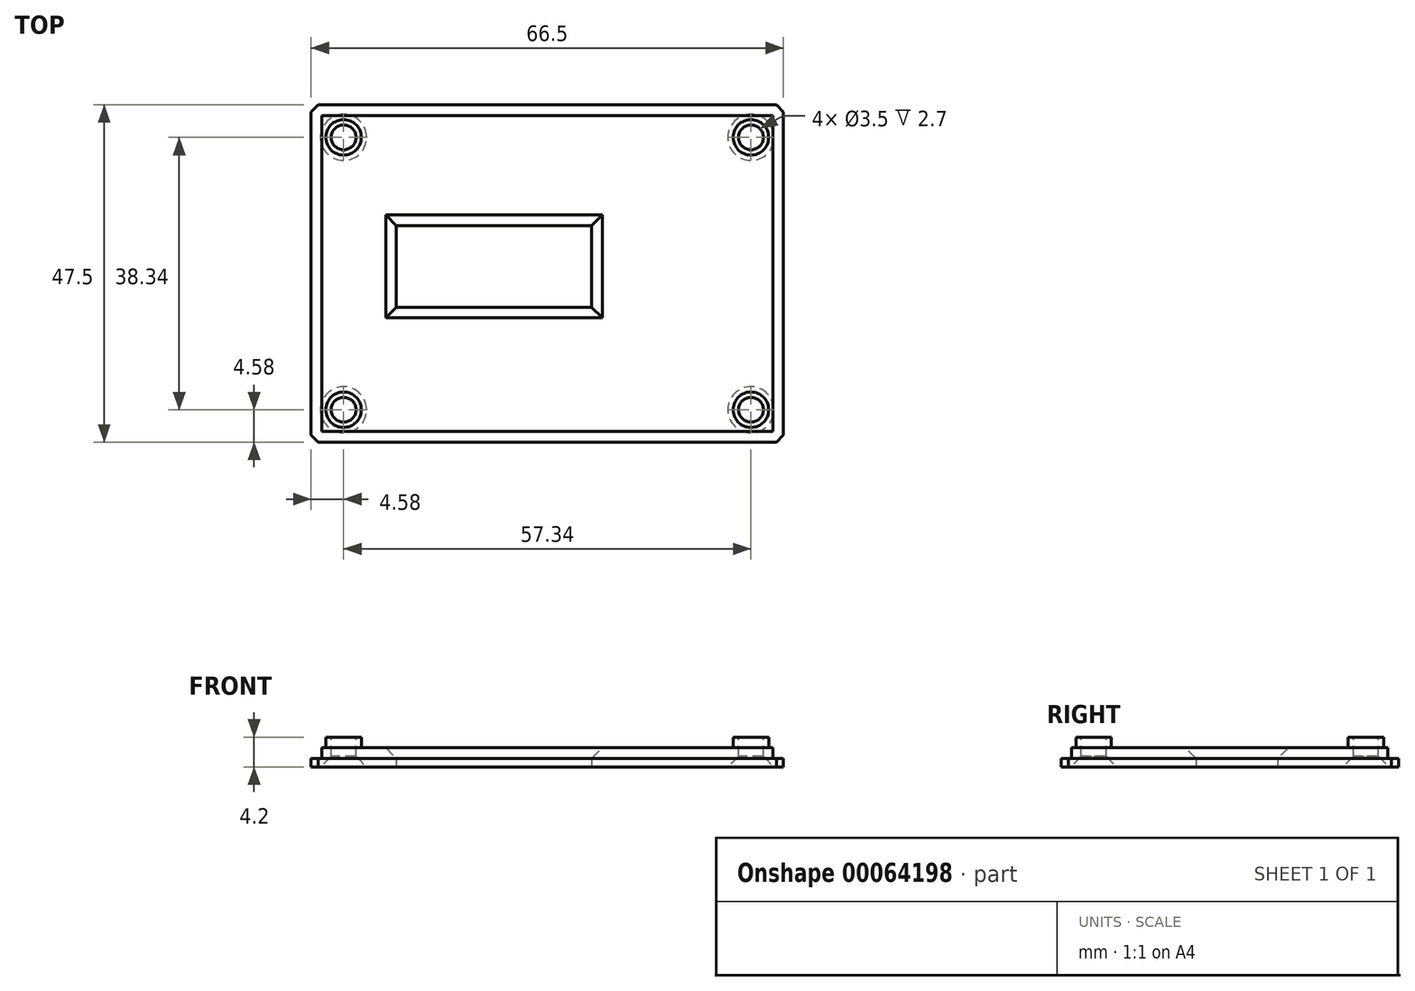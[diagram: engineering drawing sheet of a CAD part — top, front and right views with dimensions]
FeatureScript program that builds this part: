
annotation { "Feature Type Name" : "Feature", "Feature Type Description" : "" }
export const myFeature = defineFeature(function(context is Context, id is Id, definition is map)
    precondition{}
    {
        {
            var Q0;
            Q0=qCreatedBy(makeId("Top.planeOp"),FACE);
            var sketch = newSketch(context, id + "F0", { "sketchPlane" : qUnion([Q0])});
            skLineSegment(sketch, "E0.rect.bottom", {"start": v(33.25, 23.75) * mm, "end": v(-33.25, 23.75) * mm});
            skLineSegment(sketch, "E0.rect.top", {"start": v(33.25, -23.75) * mm, "end": v(-33.25, -23.75) * mm});
            skLineSegment(sketch, "E0.rect.left", {"start": v(33.25, 23.75) * mm, "end": v(33.25, -23.75) * mm});
            skLineSegment(sketch, "E0.rect.right", {"start": v(-33.25, 23.75) * mm, "end": v(-33.25, -23.75) * mm});
            skPoint(sketch, "E0.rect.middle", {"position": v(0, 0) * mm});
            skSolve(sketch);
        }
        {
            var Q0;
            Q0=qSketchRegion(id+"F0",true);
            extrude(context, id + "F1", {"entities" : qUnion([Q0]), "depth" : 1.2 * mm});
        }
        {
            var Q0;
            Q0=makeQuery(id+"F1.opExtrude","CAP_FACE",FACE,{"disambiguationData":[OSD([sQuery(id+"F0.wireOp",EDGE,"E0.rect.bottom"),sQuery(id+"F0.wireOp",EDGE,"E0.rect.top"),sQuery(id+"F0.wireOp",EDGE,"E0.rect.left"),sQuery(id+"F0.wireOp",EDGE,"E0.rect.right")])],"isStart":false});
            var sketch = newSketch(context, id + "F2", { "sketchPlane" : qUnion([Q0])});
            skLineSegment(sketch, "E1.bottom", {"start": v(-31.75, 22.25) * mm, "end": v(31.75, 22.25) * mm});
            skLineSegment(sketch, "E1.top", {"start": v(-31.75, -22.25) * mm, "end": v(31.75, -22.25) * mm});
            skLineSegment(sketch, "E1.left", {"start": v(-31.75, 22.25) * mm, "end": v(-31.75, -22.25) * mm});
            skLineSegment(sketch, "E1.right", {"start": v(31.75, 22.25) * mm, "end": v(31.75, -22.25) * mm});
            skSolve(sketch);
        }
        {
            var Q0;
            Q0=qSketchRegion(id+"F2",true);
            extrude(context, id + "F3", {"entities" : qUnion([Q0]), "operationType" : NewBodyOperationType.ADD, "depth" : 1.5 * mm});
        }
        {
            var Q0;
            Q0=makeQuery(id+"F3.opExtrude","CAP_FACE",FACE,{"disambiguationData":[OSD([sQuery(id+"F2.wireOp",EDGE,"E1.bottom"),sQuery(id+"F2.wireOp",EDGE,"E1.top"),sQuery(id+"F2.wireOp",EDGE,"E1.left"),sQuery(id+"F2.wireOp",EDGE,"E1.right")])],"isStart":false});
            var sketch = newSketch(context, id + "F4", { "sketchPlane" : qUnion([Q0])});
            skCircle(sketch, "E2", {"center": v(-28.67, -19.17) * mm, "radius": 2.5 * mm});
            skCircle(sketch, "E3.0.MirrorC", {"center": v(28.67, -19.17) * mm, "radius": 2.5 * mm});
            skCircle(sketch, "E4.0.MirrorC", {"center": v(-28.67, 19.17) * mm, "radius": 2.5 * mm});
            skCircle(sketch, "E5.0.MirrorC", {"center": v(28.67, 19.17) * mm, "radius": 2.5 * mm});
            skSolve(sketch);
        }
        {
            var Q0;
            Q0=qSketchRegion(id+"F4",true);
            extrude(context, id + "F5", {"entities" : qUnion([Q0]), "operationType" : NewBodyOperationType.ADD, "depth" : 1.5 * mm});
        }
        {
            var Q0;
            Q0=makeQuery(id+"F5.opExtrude","CAP_FACE",FACE,{"disambiguationData":[OSD([sQuery(id+"F4.wireOp",EDGE,"E2")])],"isStart":false});
            var sketch = newSketch(context, id + "F6", { "sketchPlane" : qUnion([Q0])});
            skCircle(sketch, "E6", {"center": v(-28.67, -19.17) * mm, "radius": 1.75 * mm});
            skCircle(sketch, "E7.0.MirrorC", {"center": v(28.67, -19.17) * mm, "radius": 1.75 * mm});
            skCircle(sketch, "E8.0.MirrorC", {"center": v(-28.67, 19.17) * mm, "radius": 1.75 * mm});
            skCircle(sketch, "E9.0.MirrorC", {"center": v(28.67, 19.17) * mm, "radius": 1.75 * mm});
            skSolve(sketch);
        }
        {
            var Q0;
            Q0=qSketchRegion(id+"F6",true);
            extrude(context, id + "F7", {"entities" : qUnion([Q0]), "operationType" : NewBodyOperationType.REMOVE, "endBound" : BoundingType.THROUGH_ALL, "oppositeDirection" : true, "depth" : 25 * mm});
        }
        {
            var Q0;
            Q0=makeQuery(id+"F1.opExtrude","CAP_FACE",FACE,{"disambiguationData":[OSD([sQuery(id+"F0.wireOp",EDGE,"E0.rect.bottom"),sQuery(id+"F0.wireOp",EDGE,"E0.rect.top"),sQuery(id+"F0.wireOp",EDGE,"E0.rect.left"),sQuery(id+"F0.wireOp",EDGE,"E0.rect.right")])],"isStart":true});
            var sketch = newSketch(context, id + "F8", { "sketchPlane" : qUnion([Q0])});
            skLineSegment(sketch, "E10.bottom", {"start": v(-21.25, 4.75) * mm, "end": v(6.25, 4.75) * mm});
            skLineSegment(sketch, "E10.top", {"start": v(-21.25, -6.75) * mm, "end": v(6.25, -6.75) * mm});
            skLineSegment(sketch, "E10.left", {"start": v(-21.25, 4.75) * mm, "end": v(-21.25, -6.75) * mm});
            skLineSegment(sketch, "E10.right", {"start": v(6.25, 4.75) * mm, "end": v(6.25, -6.75) * mm});
            skSolve(sketch);
        }
        {
            var Q0;
            Q0=qSketchRegion(id+"F8",true);
            extrude(context, id + "F9", {"entities" : qUnion([Q0]), "operationType" : NewBodyOperationType.REMOVE, "endBound" : BoundingType.THROUGH_ALL, "oppositeDirection" : true, "depth" : 25 * mm});
        }
        {
            var Q0;
            Q0=makeQuery(id+"F7.boolean.opBoolean","INTERSECT",EDGE,{"derivedFrom":[makeQuery(id+"F1.opExtrude","CAP_FACE",FACE,{"disambiguationData":[OSD([sQuery(id+"F0.wireOp",EDGE,"E0.rect.bottom"),sQuery(id+"F0.wireOp",EDGE,"E0.rect.top"),sQuery(id+"F0.wireOp",EDGE,"E0.rect.left"),sQuery(id+"F0.wireOp",EDGE,"E0.rect.right")])],"isStart":true}),makeQuery(id+"F7.opExtrude","SWEPT_FACE",FACE,{"disambiguationData":[OSD([sQuery(id+"F6.wireOp",EDGE,"E6")])]})]});
            var Q1;
            Q1=makeQuery(id+"F7.boolean.opBoolean","INTERSECT",EDGE,{"derivedFrom":[makeQuery(id+"F1.opExtrude","CAP_FACE",FACE,{"disambiguationData":[OSD([sQuery(id+"F0.wireOp",EDGE,"E0.rect.bottom"),sQuery(id+"F0.wireOp",EDGE,"E0.rect.top"),sQuery(id+"F0.wireOp",EDGE,"E0.rect.left"),sQuery(id+"F0.wireOp",EDGE,"E0.rect.right")])],"isStart":true}),makeQuery(id+"F7.opExtrude","SWEPT_FACE",FACE,{"disambiguationData":[OSD([sQuery(id+"F6.wireOp",EDGE,"E7.0.MirrorC")])]})]});
            var Q2;
            Q2=makeQuery(id+"F7.boolean.opBoolean","INTERSECT",EDGE,{"derivedFrom":[makeQuery(id+"F1.opExtrude","CAP_FACE",FACE,{"disambiguationData":[OSD([sQuery(id+"F0.wireOp",EDGE,"E0.rect.bottom"),sQuery(id+"F0.wireOp",EDGE,"E0.rect.top"),sQuery(id+"F0.wireOp",EDGE,"E0.rect.left"),sQuery(id+"F0.wireOp",EDGE,"E0.rect.right")])],"isStart":true}),makeQuery(id+"F7.opExtrude","SWEPT_FACE",FACE,{"disambiguationData":[OSD([sQuery(id+"F6.wireOp",EDGE,"E9.0.MirrorC")])]})]});
            var Q3;
            Q3=makeQuery(id+"F7.boolean.opBoolean","INTERSECT",EDGE,{"derivedFrom":[makeQuery(id+"F1.opExtrude","CAP_FACE",FACE,{"disambiguationData":[OSD([sQuery(id+"F0.wireOp",EDGE,"E0.rect.bottom"),sQuery(id+"F0.wireOp",EDGE,"E0.rect.top"),sQuery(id+"F0.wireOp",EDGE,"E0.rect.left"),sQuery(id+"F0.wireOp",EDGE,"E0.rect.right")])],"isStart":true}),makeQuery(id+"F7.opExtrude","SWEPT_FACE",FACE,{"disambiguationData":[OSD([sQuery(id+"F6.wireOp",EDGE,"E8.0.MirrorC")])]})]});
            chamfer(context, id + "F10", {"entities" : qUnion([Q0, Q1, Q2, Q3]), "width" : 1.5 * mm, "tangentPropagation" : true});
        }
        {
            var Q0;
            Q0=makeQuery(id+"F1.opExtrude","SWEPT_EDGE",EDGE,{"disambiguationData":[OSD([sQuery(id+"F0.wireOp",EDGE,"E0.rect.top"),sQuery(id+"F0.wireOp",EDGE,"E0.rect.right")])]});
            var Q1;
            Q1=makeQuery(id+"F1.opExtrude","SWEPT_EDGE",EDGE,{"disambiguationData":[OSD([sQuery(id+"F0.wireOp",EDGE,"E0.rect.bottom"),sQuery(id+"F0.wireOp",EDGE,"E0.rect.right")])]});
            var Q2;
            Q2=makeQuery(id+"F1.opExtrude","SWEPT_EDGE",EDGE,{"disambiguationData":[OSD([sQuery(id+"F0.wireOp",EDGE,"E0.rect.bottom"),sQuery(id+"F0.wireOp",EDGE,"E0.rect.left")])]});
            var Q3;
            Q3=makeQuery(id+"F1.opExtrude","SWEPT_EDGE",EDGE,{"disambiguationData":[OSD([sQuery(id+"F0.wireOp",EDGE,"E0.rect.top"),sQuery(id+"F0.wireOp",EDGE,"E0.rect.left")])]});
            chamfer(context, id + "F11", {"entities" : qUnion([Q0, Q1, Q2, Q3]), "width" : 1 * mm, "tangentPropagation" : true});
        }
        {
            var Q0;
            Q0=makeQuery(id+"F9.boolean.opBoolean","INTERSECT",EDGE,{"derivedFrom":[makeQuery(id+"F3.opExtrude","CAP_FACE",FACE,{"disambiguationData":[OSD([sQuery(id+"F2.wireOp",EDGE,"E1.bottom"),sQuery(id+"F2.wireOp",EDGE,"E1.top"),sQuery(id+"F2.wireOp",EDGE,"E1.left"),sQuery(id+"F2.wireOp",EDGE,"E1.right")])],"isStart":false}),makeQuery(id+"F9.opExtrude","SWEPT_FACE",FACE,{"disambiguationData":[OSD([sQuery(id+"F8.wireOp",EDGE,"E10.top")])]})]});
            var Q1;
            Q1=makeQuery(id+"F9.boolean.opBoolean","INTERSECT",EDGE,{"derivedFrom":[makeQuery(id+"F3.opExtrude","CAP_FACE",FACE,{"disambiguationData":[OSD([sQuery(id+"F2.wireOp",EDGE,"E1.bottom"),sQuery(id+"F2.wireOp",EDGE,"E1.top"),sQuery(id+"F2.wireOp",EDGE,"E1.left"),sQuery(id+"F2.wireOp",EDGE,"E1.right")])],"isStart":false}),makeQuery(id+"F9.opExtrude","SWEPT_FACE",FACE,{"disambiguationData":[OSD([sQuery(id+"F8.wireOp",EDGE,"E10.right")])]})]});
            var Q2;
            Q2=makeQuery(id+"F9.boolean.opBoolean","INTERSECT",EDGE,{"derivedFrom":[makeQuery(id+"F3.opExtrude","CAP_FACE",FACE,{"disambiguationData":[OSD([sQuery(id+"F2.wireOp",EDGE,"E1.bottom"),sQuery(id+"F2.wireOp",EDGE,"E1.top"),sQuery(id+"F2.wireOp",EDGE,"E1.left"),sQuery(id+"F2.wireOp",EDGE,"E1.right")])],"isStart":false}),makeQuery(id+"F9.opExtrude","SWEPT_FACE",FACE,{"disambiguationData":[OSD([sQuery(id+"F8.wireOp",EDGE,"E10.bottom")])]})]});
            var Q3;
            Q3=makeQuery(id+"F9.boolean.opBoolean","INTERSECT",EDGE,{"derivedFrom":[makeQuery(id+"F3.opExtrude","CAP_FACE",FACE,{"disambiguationData":[OSD([sQuery(id+"F2.wireOp",EDGE,"E1.bottom"),sQuery(id+"F2.wireOp",EDGE,"E1.top"),sQuery(id+"F2.wireOp",EDGE,"E1.left"),sQuery(id+"F2.wireOp",EDGE,"E1.right")])],"isStart":false}),makeQuery(id+"F9.opExtrude","SWEPT_FACE",FACE,{"disambiguationData":[OSD([sQuery(id+"F8.wireOp",EDGE,"E10.left")])]})]});
            chamfer(context, id + "F12", {"entities" : qUnion([Q0, Q1, Q2, Q3]), "width" : 1.5 * mm, "tangentPropagation" : true});
        }
    });
